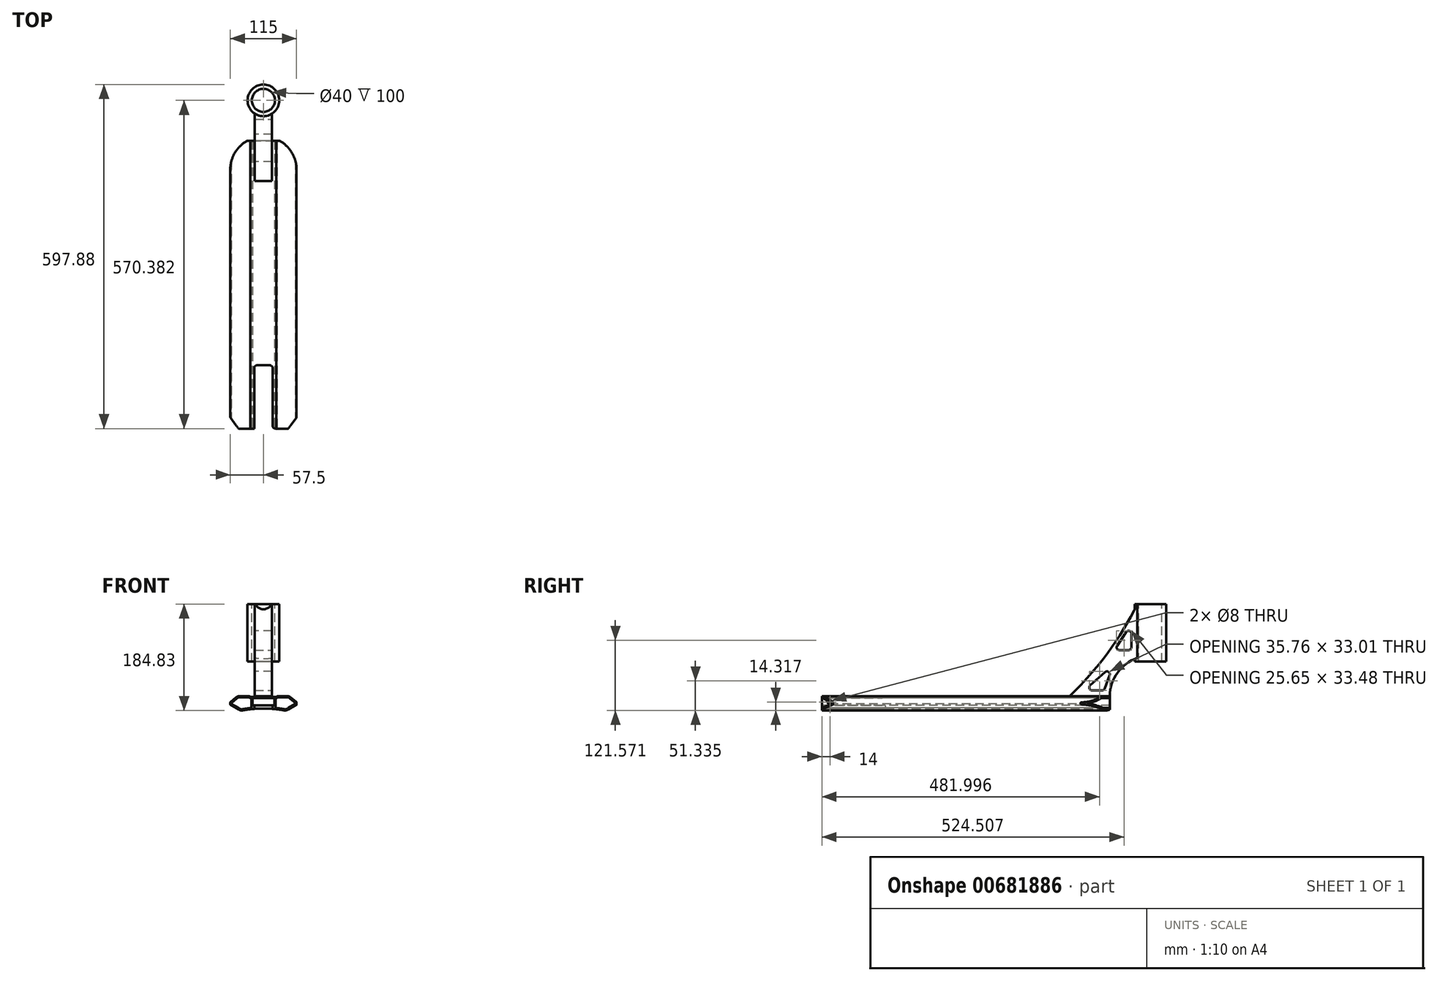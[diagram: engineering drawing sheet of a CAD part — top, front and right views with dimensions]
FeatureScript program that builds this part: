
annotation { "Feature Type Name" : "Feature", "Feature Type Description" : "" }
export const myFeature = defineFeature(function(context is Context, id is Id, definition is map)
    precondition{}
    {
        {
            var Q0;
            Q0=qCreatedBy(makeId("Front.planeOp"),FACE);
            var sketch = newSketch(context, id + "F0", { "sketchPlane" : qUnion([Q0])});
            skLineSegment(sketch, "E0", {"start": v(0, 0) * mm, "end": v(0, 38.3) * mm, "construction": true});
            skLineSegment(sketch, "E1", {"start": v(0, 20.02) * mm, "end": v(22.5, 20.02) * mm});
            skLineSegment(sketch, "E2", {"start": v(22.5, 20.02) * mm, "end": v(22.5, 21.32) * mm});
            skLineSegment(sketch, "E3", {"start": v(22.5, 21.32) * mm, "end": v(44.7, 21.32) * mm});
            skLineSegment(sketch, "E4", {"start": v(44.7, 21.32) * mm, "end": v(57.5, 10.57) * mm});
            skLineSegment(sketch, "E5", {"start": v(57.5, 10.57) * mm, "end": v(57.5, 6.57) * mm});
            skLineSegment(sketch, "E6", {"start": v(57.5, 6.57) * mm, "end": v(39.22, -3.98) * mm});
            skLineSegment(sketch, "E7.MirrorCS", {"start": v(0, 20.02) * mm, "end": v(-22.5, 20.02) * mm});
            skLineSegment(sketch, "E8.MirrorCS", {"start": v(-22.5, 21.32) * mm, "end": v(-44.7, 21.32) * mm});
            skLineSegment(sketch, "E9.MirrorCS", {"start": v(-22.5, 20.02) * mm, "end": v(-22.5, 21.32) * mm});
            skLineSegment(sketch, "E10.MirrorCS", {"start": v(-44.7, 21.32) * mm, "end": v(-57.5, 10.57) * mm});
            skLineSegment(sketch, "E11.MirrorCS", {"start": v(-57.5, 10.57) * mm, "end": v(-57.5, 6.57) * mm});
            skLineSegment(sketch, "E12.MirrorCS", {"start": v(-57.5, 6.57) * mm, "end": v(-39.22, -3.98) * mm});
            skArc(sketch, "E13", {"start": v(39.22, -3.98) * mm, "mid": v(0, -0.1) * mm, "end": v(-39.22, -3.98) * mm});
            skSolve(sketch);
        }
        {
            var Q0;
            Q0 = qSketchRegion(id + "F0", true);
            extrude(context, id + "F1", {"entities" : qUnion([Q0]), "endBound" : BoundingType.SYMMETRIC, "depth" : 500 * mm, "offsetDistance" : 25 * mm});
        }
        {
            var Q0;
            Q0=qCreatedBy(makeId("Front.planeOp"),FACE);
            var sketch = newSketch(context, id + "F2", { "sketchPlane" : qUnion([Q0])});
            skLineSegment(sketch, "E14", {"start": v(-19, 18.02) * mm, "end": v(19, 18.02) * mm});
            skLineSegment(sketch, "E15", {"start": v(19, 18.02) * mm, "end": v(19, 5.02) * mm});
            skLineSegment(sketch, "E16", {"start": v(19, 5.02) * mm, "end": v(-19, 5.02) * mm});
            skLineSegment(sketch, "E17", {"start": v(-19, 5.02) * mm, "end": v(-19, 18.02) * mm});
            skSolve(sketch);
        }
        {
            var Q0;
            Q0 = qSketchRegion(id + "F2", true);
            extrude(context, id + "F3", {"entities" : qUnion([Q0]), "operationType" : NewBodyOperationType.REMOVE, "endBound" : BoundingType.SYMMETRIC, "oppositeDirection" : true, "depth" : 500 * mm, "offsetDistance" : 25 * mm});
        }
        {
            var Q0;
            Q0=makeQuery(id+"F1.opExtrude","SWEPT_EDGE",EDGE,{"disambiguationData":[OSD([sQuery(id+"F0.wireOp",EDGE,"E2"),sQuery(id+"F0.wireOp",EDGE,"E3")])]});
            var Q1;
            Q1=makeQuery(id+"F1.opExtrude","SWEPT_EDGE",EDGE,{"disambiguationData":[OSD([sQuery(id+"F0.wireOp",EDGE,"E9.MirrorCS"),sQuery(id+"F0.wireOp",EDGE,"E8.MirrorCS")])]});
            fillet(context, id + "F4", {"entities" : qUnion([Q0, Q1]), "radius" : 5 * mm, "tangentPropagation" : true, "allowEdgeOverflow" : false});
        }
        {
            var Q0;
            Q0=makeQuery(id+"F1.opExtrude","SWEPT_EDGE",EDGE,{"disambiguationData":[OSD([sQuery(id+"F0.wireOp",EDGE,"E8.MirrorCS"),sQuery(id+"F0.wireOp",EDGE,"E10.MirrorCS")])]});
            var Q1;
            Q1=makeQuery(id+"F1.opExtrude","SWEPT_EDGE",EDGE,{"disambiguationData":[OSD([sQuery(id+"F0.wireOp",EDGE,"E3"),sQuery(id+"F0.wireOp",EDGE,"E4")])]});
            var Q2;
            Q2=makeQuery(id+"F1.opExtrude","SWEPT_EDGE",EDGE,{"disambiguationData":[OSD([sQuery(id+"F0.wireOp",EDGE,"E12.MirrorCS"),sQuery(id+"F0.wireOp",EDGE,"E13")])]});
            var Q3;
            Q3=makeQuery(id+"F1.opExtrude","SWEPT_EDGE",EDGE,{"disambiguationData":[OSD([sQuery(id+"F0.wireOp",EDGE,"E6"),sQuery(id+"F0.wireOp",EDGE,"E13")])]});
            fillet(context, id + "F5", {"entities" : qUnion([Q0, Q1, Q2, Q3]), "radius" : 9 * mm, "tangentPropagation" : true, "allowEdgeOverflow" : false});
        }
        {
            var Q0;
            Q0=makeQuery(id+"F1.opExtrude","SWEPT_EDGE",EDGE,{"disambiguationData":[OSD([sQuery(id+"F0.wireOp",EDGE,"E6"),sQuery(id+"F0.wireOp",EDGE,"E5")])]});
            var Q1;
            Q1=makeQuery(id+"F1.opExtrude","SWEPT_EDGE",EDGE,{"disambiguationData":[OSD([sQuery(id+"F0.wireOp",EDGE,"E4"),sQuery(id+"F0.wireOp",EDGE,"E5")])]});
            var Q2;
            Q2=makeQuery(id+"F1.opExtrude","SWEPT_EDGE",EDGE,{"disambiguationData":[OSD([sQuery(id+"F0.wireOp",EDGE,"E10.MirrorCS"),sQuery(id+"F0.wireOp",EDGE,"E11.MirrorCS")])]});
            var Q3;
            Q3=makeQuery(id+"F1.opExtrude","SWEPT_EDGE",EDGE,{"disambiguationData":[OSD([sQuery(id+"F0.wireOp",EDGE,"E11.MirrorCS"),sQuery(id+"F0.wireOp",EDGE,"E12.MirrorCS")])]});
            fillet(context, id + "F6", {"entities" : qUnion([Q0, Q1, Q2, Q3]), "radius" : 1 * mm, "tangentPropagation" : true, "allowEdgeOverflow" : false});
        }
        {
            var Q0;
            Q0=makeQuery(id+"F1.opExtrude","CAP_FACE",FACE,{"disambiguationData":[OSD([sQuery(id+"F0.wireOp",EDGE,"E1"),sQuery(id+"F0.wireOp",EDGE,"E2"),sQuery(id+"F0.wireOp",EDGE,"E3"),sQuery(id+"F0.wireOp",EDGE,"E4"),sQuery(id+"F0.wireOp",EDGE,"E6"),sQuery(id+"F0.wireOp",EDGE,"E7.MirrorCS"),sQuery(id+"F0.wireOp",EDGE,"E9.MirrorCS"),sQuery(id+"F0.wireOp",EDGE,"E8.MirrorCS"),sQuery(id+"F0.wireOp",EDGE,"E10.MirrorCS"),sQuery(id+"F0.wireOp",EDGE,"E11.MirrorCS"),sQuery(id+"F0.wireOp",EDGE,"E12.MirrorCS"),sQuery(id+"F0.wireOp",EDGE,"E5"),sQuery(id+"F0.wireOp",EDGE,"E13")])],"isStart":false});
            var sketch = newSketch(context, id + "F7", { "sketchPlane" : qUnion([Q0])});
            skArc(sketch, "E18.0", {"start": v(-21, 0.8) * mm, "mid": v(-28.7, -0.15) * mm, "end": v(-36.36, -1.4) * mm});
            skArc(sketch, "E18.1", {"start": v(-41.12, -0.57) * mm, "mid": v(-38.81, -1.4) * mm, "end": v(-36.36, -1.4) * mm});
            skLineSegment(sketch, "E18.2", {"start": v(-55.5, 7.73) * mm, "end": v(-41.12, -0.57) * mm});
            skArc(sketch, "E18.4", {"start": v(-23.4, 18.02) * mm, "mid": v(-24.47, 18.97) * mm, "end": v(-25.86, 19.32) * mm});
            skLineSegment(sketch, "E18.5", {"start": v(-25.86, 19.32) * mm, "end": v(-41.42, 19.32) * mm});
            skArc(sketch, "E18.6", {"start": v(-41.42, 19.32) * mm, "mid": v(-43.81, 18.9) * mm, "end": v(-45.92, 17.68) * mm});
            skLineSegment(sketch, "E18.7", {"start": v(-45.92, 17.68) * mm, "end": v(-55.76, 9.42) * mm});
            skLineSegment(sketch, "E19.0", {"start": v(-21, 0.8) * mm, "end": v(-21, 18.02) * mm});
            skLineSegment(sketch, "E20.0", {"start": v(-23.4, 18.02) * mm, "end": v(-21, 18.02) * mm});
            skPoint(sketch, "E21.startSnap0", {"position": v(-55.5, 8.69) * mm});
            skArc(sketch, "E22", {"start": v(-55.76, 9.42) * mm, "mid": v(-56.1, 8.5) * mm, "end": v(-55.5, 7.73) * mm});
            skLineSegment(sketch, "E23", {"start": v(0, 55.9) * mm, "end": v(0, 0) * mm, "construction": true});
            skLineSegment(sketch, "E24.MirrorCS", {"start": v(23.4, 18.02) * mm, "end": v(21, 18.02) * mm});
            skLineSegment(sketch, "E25.MirrorCS", {"start": v(21, 0.8) * mm, "end": v(21, 18.02) * mm});
            skArc(sketch, "E26.MirrorCS", {"start": v(21, 0.8) * mm, "mid": v(28.7, -0.15) * mm, "end": v(36.36, -1.4) * mm});
            skArc(sketch, "E27.MirrorCS", {"start": v(41.12, -0.57) * mm, "mid": v(38.81, -1.4) * mm, "end": v(36.36, -1.4) * mm});
            skLineSegment(sketch, "E28.MirrorCS", {"start": v(55.5, 7.73) * mm, "end": v(41.12, -0.57) * mm});
            skArc(sketch, "E29.MirrorCS", {"start": v(55.76, 9.42) * mm, "mid": v(56.1, 8.5) * mm, "end": v(55.5, 7.73) * mm});
            skLineSegment(sketch, "E30.MirrorCS", {"start": v(45.92, 17.68) * mm, "end": v(55.76, 9.42) * mm});
            skArc(sketch, "E31.MirrorCS", {"start": v(41.42, 19.32) * mm, "mid": v(43.81, 18.9) * mm, "end": v(45.92, 17.68) * mm});
            skLineSegment(sketch, "E32.MirrorCS", {"start": v(25.86, 19.32) * mm, "end": v(41.42, 19.32) * mm});
            skArc(sketch, "E33.MirrorCS", {"start": v(23.4, 18.02) * mm, "mid": v(24.47, 18.97) * mm, "end": v(25.86, 19.32) * mm});
            skSolve(sketch);
        }
        {
            var Q0;
            Q0=makeQuery(id+"F7.imprint","IMPRINT",FACE,{"disambiguationData":[TD([[makeQuery(id+"F7.imprint","IMPRINT",EDGE,{"derivedFrom":sQuery(id+"F7.wireOp",EDGE,"E24.MirrorCS")}),1.0]])]});
            var Q1;
            Q1=makeQuery(id+"F7.imprint","IMPRINT",FACE,{"disambiguationData":[TD([[makeQuery(id+"F7.imprint","IMPRINT",EDGE,{"derivedFrom":sQuery(id+"F7.wireOp",EDGE,"E18.0")}),-1.0]])]});
            extrude(context, id + "F8", {"entities" : qUnion([Q0, Q1]), "operationType" : NewBodyOperationType.REMOVE, "endBound" : BoundingType.THROUGH_ALL, "oppositeDirection" : true, "depth" : 25 * mm, "offsetDistance" : 25 * mm});
        }
        {
            var Q0;
            Q0=qCreatedBy(makeId("Top.planeOp"),FACE);
            var sketch = newSketch(context, id + "F9", { "sketchPlane" : qUnion([Q0])});
            skArc(sketch, "E34", {"start": v(57.5, 199.3) * mm, "mid": v(0.35, 257.5) * mm, "end": v(-57.5, 200) * mm});
            skLineSegment(sketch, "E35", {"start": v(-57.5, 200) * mm, "end": v(-57.5, 280) * mm});
            skLineSegment(sketch, "E36", {"start": v(58.48, 280) * mm, "end": v(57.5, 199.3) * mm});
            skLineSegment(sketch, "E37", {"start": v(-57.5, 280) * mm, "end": v(58.48, 280) * mm});
            skSolve(sketch);
        }
        {
            var Q0;
            Q0 = qSketchRegion(id + "F9", true);
            extrude(context, id + "F10", {"entities" : qUnion([Q0]), "operationType" : NewBodyOperationType.REMOVE, "endBound" : BoundingType.THROUGH_ALL, "depth" : 25 * mm, "offsetDistance" : 25 * mm, "hasSecondDirection" : true, "secondDirectionBound" : SecondDirectionBoundingType.THROUGH_ALL, "secondDirectionOppositeDirection" : true, "secondDirectionDepth" : 25 * mm});
        }
        {
            var Q0;
            Q0=qCreatedBy(makeId("Top.planeOp"),FACE);
            var sketch = newSketch(context, id + "F11", { "sketchPlane" : qUnion([Q0])});
            skLineSegment(sketch, "E38", {"start": v(-68, -216) * mm, "end": v(-68, -346) * mm});
            skLineSegment(sketch, "E39", {"start": v(-68, -346) * mm, "end": v(68, -346) * mm});
            skLineSegment(sketch, "E40", {"start": v(68, -346) * mm, "end": v(68, -216) * mm});
            skLineSegment(sketch, "E41", {"start": v(68, -216) * mm, "end": v(43.3, -250) * mm});
            skLineSegment(sketch, "E42", {"start": v(43.3, -250) * mm, "end": v(16, -250) * mm});
            skLineSegment(sketch, "E43", {"start": v(16, -250) * mm, "end": v(16, -140) * mm});
            skLineSegment(sketch, "E44", {"start": v(16, -140) * mm, "end": v(-16, -140) * mm});
            skLineSegment(sketch, "E45", {"start": v(-16, -140) * mm, "end": v(-16, -250) * mm});
            skLineSegment(sketch, "E46", {"start": v(-16, -250) * mm, "end": v(-43.3, -250) * mm});
            skLineSegment(sketch, "E47", {"start": v(-43.3, -250) * mm, "end": v(-68, -216) * mm});
            skSolve(sketch);
        }
        {
            var Q0;
            Q0 = qSketchRegion(id + "F11", true);
            extrude(context, id + "F12", {"entities" : qUnion([Q0]), "operationType" : NewBodyOperationType.REMOVE, "endBound" : BoundingType.THROUGH_ALL, "depth" : 25 * mm, "offsetDistance" : 25 * mm, "hasSecondDirection" : true, "secondDirectionBound" : SecondDirectionBoundingType.THROUGH_ALL, "secondDirectionOppositeDirection" : true, "secondDirectionDepth" : 25 * mm});
        }
        {
            var Q0;
            {var subQ2=sQuery(id+"F11.wireOp",EDGE,"E45");Q0=makeQuery(id+"F12.boolean.opBoolean","COPY",EDGE,{"disambiguationData":[TD([makeQuery(id+"F3.boolean.opBoolean","COPY",FACE,{"derivedFrom":makeQuery(id+"F3.opExtrude","SWEPT_FACE",FACE,{"disambiguationData":[OSD([sQuery(id+"F2.wireOp",EDGE,"E14")])]})})])],"derivedFrom":makeQuery(id+"F12.opExtrude","SWEPT_EDGE",EDGE,{"disambiguationData":[OSD([subQ2,sQuery(id+"F11.wireOp",EDGE,"E46")])]})});}
            var Q1;
            {var subQ0=sQuery(id+"F0.wireOp",EDGE,"E13");var subQ1=sQuery(id+"F11.wireOp",EDGE,"E45");Q1=makeQuery(id+"F12.boolean.opBoolean","COPY",EDGE,{"disambiguationData":[TD([makeQuery(id+"F1.opExtrude","SWEPT_FACE",FACE,{"disambiguationData":[OSD([subQ0])]})])],"derivedFrom":makeQuery(id+"F12.opExtrude","SWEPT_EDGE",EDGE,{"disambiguationData":[OSD([subQ1,sQuery(id+"F11.wireOp",EDGE,"E46")])]})});}
            var Q2;
            {var subQ0=sQuery(id+"F11.wireOp",EDGE,"E44");var subQ1=sQuery(id+"F11.wireOp",EDGE,"E45");Q2=makeQuery(id+"F12.boolean.opBoolean","COPY",EDGE,{"disambiguationData":[TD([makeQuery(id+"F3.boolean.opBoolean","COPY",FACE,{"derivedFrom":makeQuery(id+"F3.opExtrude","SWEPT_FACE",FACE,{"disambiguationData":[OSD([sQuery(id+"F2.wireOp",EDGE,"E14")])]})})])],"derivedFrom":makeQuery(id+"F12.opExtrude","SWEPT_EDGE",EDGE,{"disambiguationData":[OSD([subQ0,subQ1])]})});}
            var Q3;
            {var subQ0=sQuery(id+"F11.wireOp",EDGE,"E44");var subQ1=sQuery(id+"F11.wireOp",EDGE,"E45");Q3=makeQuery(id+"F12.boolean.opBoolean","COPY",EDGE,{"disambiguationData":[TD([makeQuery(id+"F1.opExtrude","SWEPT_FACE",FACE,{"disambiguationData":[OSD([sQuery(id+"F0.wireOp",EDGE,"E13")])]})])],"derivedFrom":makeQuery(id+"F12.opExtrude","SWEPT_EDGE",EDGE,{"disambiguationData":[OSD([subQ0,subQ1])]})});}
            var Q4;
            {var subQ0=sQuery(id+"F11.wireOp",EDGE,"E43");var subQ1=sQuery(id+"F11.wireOp",EDGE,"E44");Q4=makeQuery(id+"F12.boolean.opBoolean","COPY",EDGE,{"disambiguationData":[TD([makeQuery(id+"F1.opExtrude","SWEPT_FACE",FACE,{"disambiguationData":[OSD([sQuery(id+"F0.wireOp",EDGE,"E13")])]})])],"derivedFrom":makeQuery(id+"F12.opExtrude","SWEPT_EDGE",EDGE,{"disambiguationData":[OSD([subQ0,subQ1])]})});}
            var Q5;
            {var subQ0=sQuery(id+"F11.wireOp",EDGE,"E43");var subQ1=sQuery(id+"F11.wireOp",EDGE,"E44");Q5=makeQuery(id+"F12.boolean.opBoolean","COPY",EDGE,{"disambiguationData":[TD([makeQuery(id+"F3.boolean.opBoolean","COPY",FACE,{"derivedFrom":makeQuery(id+"F3.opExtrude","SWEPT_FACE",FACE,{"disambiguationData":[OSD([sQuery(id+"F2.wireOp",EDGE,"E14")])]})})])],"derivedFrom":makeQuery(id+"F12.opExtrude","SWEPT_EDGE",EDGE,{"disambiguationData":[OSD([subQ0,subQ1])]})});}
            var Q6;
            {var subQ2=sQuery(id+"F11.wireOp",EDGE,"E43");Q6=makeQuery(id+"F12.boolean.opBoolean","COPY",EDGE,{"disambiguationData":[TD([makeQuery(id+"F3.boolean.opBoolean","COPY",FACE,{"derivedFrom":makeQuery(id+"F3.opExtrude","SWEPT_FACE",FACE,{"disambiguationData":[OSD([sQuery(id+"F2.wireOp",EDGE,"E14")])]})})])],"derivedFrom":makeQuery(id+"F12.opExtrude","SWEPT_EDGE",EDGE,{"disambiguationData":[OSD([sQuery(id+"F11.wireOp",EDGE,"E42"),subQ2])]})});}
            var Q7;
            {var subQ0=sQuery(id+"F0.wireOp",EDGE,"E13");var subQ1=sQuery(id+"F11.wireOp",EDGE,"E43");Q7=makeQuery(id+"F12.boolean.opBoolean","COPY",EDGE,{"disambiguationData":[TD([makeQuery(id+"F1.opExtrude","SWEPT_FACE",FACE,{"disambiguationData":[OSD([subQ0])]})])],"derivedFrom":makeQuery(id+"F12.opExtrude","SWEPT_EDGE",EDGE,{"disambiguationData":[OSD([sQuery(id+"F11.wireOp",EDGE,"E42"),subQ1])]})});}
            fillet(context, id + "F13", {"entities" : qUnion([Q0, Q1, Q2, Q3, Q4, Q5, Q6, Q7]), "radius" : 5 * mm, "tangentPropagation" : true, "allowEdgeOverflow" : false});
        }
        {
            var Q0;
            Q0=qCreatedBy(makeId("Right.planeOp"),FACE);
            var sketch = newSketch(context, id + "F14", { "sketchPlane" : qUnion([Q0])});
            skLineSegment(sketch, "E48", {"start": v(250, 21.32) * mm, "end": v(180, 21.32) * mm});
            skArc(sketch, "E49", {"start": v(297.38, 87.56) * mm, "mid": v(263.06, 62.04) * mm, "end": v(250, 21.32) * mm});
            skLineSegment(sketch, "E50", {"start": v(297.38, 87.56) * mm, "end": v(297.38, 81.32) * mm});
            skLineSegment(sketch, "E51", {"start": v(297.38, 81.32) * mm, "end": v(343.38, 81.32) * mm});
            skLineSegment(sketch, "E52", {"start": v(343.38, 81.32) * mm, "end": v(343.38, 181.32) * mm});
            skLineSegment(sketch, "E53", {"start": v(343.38, 181.32) * mm, "end": v(297.38, 181.32) * mm});
            skArc(sketch, "E54", {"start": v(180, 21.32) * mm, "mid": v(245.97, 95.98) * mm, "end": v(297.38, 181.32) * mm});
            skSolve(sketch);
        }
        {
            var Q0;
            Q0 = qSketchRegion(id + "F14", true);
            extrude(context, id + "F15", {"entities" : qUnion([Q0]), "operationType" : NewBodyOperationType.ADD, "endBound" : BoundingType.SYMMETRIC, "depth" : 30 * mm, "offsetDistance" : 25 * mm});
        }
        {
            var Q0;
            Q0=makeQuery(id+"F15.opExtrude","SWEPT_FACE",FACE,{"disambiguationData":[OSD([sQuery(id+"F14.wireOp",EDGE,"E53")])]});
            var sketch = newSketch(context, id + "F16", { "sketchPlane" : qUnion([Q0])});
            skCircle(sketch, "E55", {"center": v(0, 320.38) * mm, "radius": 27.5 * mm});
            skPoint(sketch, "E56.positionSnap0", {"position": v(15, 320.38) * mm});
            skSolve(sketch);
        }
        {
            var Q0;
            Q0 = qSketchRegion(id + "F16", true);
            var Q1;
            Q1=makeQuery(id+"F15.opExtrude","SWEPT_FACE",FACE,{"disambiguationData":[OSD([sQuery(id+"F14.wireOp",EDGE,"E51")])]});
            extrude(context, id + "F17", {"entities" : qUnion([Q0]), "operationType" : NewBodyOperationType.ADD, "endBound" : BoundingType.UP_TO_SURFACE, "oppositeDirection" : true, "depth" : 25 * mm, "endBoundEntityFace" : qUnion([Q1]), "offsetDistance" : 25 * mm});
        }
        {
            var Q0;
            Q0=makeQuery(id+"F17.boolean.opBoolean","MERGE",FACE,{"derivedFrom":[makeQuery(id+"F15.opExtrude","SWEPT_FACE",FACE,{"disambiguationData":[OSD([sQuery(id+"F14.wireOp",EDGE,"E53")])]}),makeQuery(id+"F17.opExtrude","CAP_FACE",FACE,{"disambiguationData":[OSD([sQuery(id+"F16.wireOp",EDGE,"E55")])],"isStart":true})]});
            var sketch = newSketch(context, id + "F18", { "sketchPlane" : qUnion([Q0])});
            skPoint(sketch, "E57", {"position": v(0, 320.38) * mm});
            skSolve(sketch);
        }
        {
            var Q0;
            Q0=sQuery(id+"F18.wireOp",VERTEX,"E57");
            var Q1;
            Q1=makeQuery(id+"F15.opExtrude","SWEPT_BODY",BODY,{"disambiguationData":[OSD([sQuery(id+"F14.wireOp",EDGE,"E48"),sQuery(id+"F14.wireOp",EDGE,"E49"),sQuery(id+"F14.wireOp",EDGE,"E50"),sQuery(id+"F14.wireOp",EDGE,"E51"),sQuery(id+"F14.wireOp",EDGE,"E52"),sQuery(id+"F14.wireOp",EDGE,"E53"),sQuery(id+"F14.wireOp",EDGE,"E54")])]});
            hole(context, id + "F19", {"style" : HoleStyle.SIMPLE, "endStyle" : HoleEndStyle.THROUGH, "holeDiameter" : 40 * mm, "majorDiameter" : 5 * mm, "isTappedThrough" : true, "tappedDepth" : 12 * mm, "tapClearance" : 3, "locations" : qUnion([Q0]), "scope" : qUnion([Q1])});
        }
        {
            var Q0;
            Q0=makeQuery(id+"F8.boolean.opBoolean","COPY",FACE,{"derivedFrom":makeQuery(id+"F8.opExtrude","SWEPT_FACE",FACE,{"disambiguationData":[OSD([sQuery(id+"F7.wireOp",EDGE,"E25.MirrorCS")])]})});
            var sketch = newSketch(context, id + "F20", { "sketchPlane" : qUnion([Q0])});
            skPoint(sketch, "E58.positionSnap0", {"position": v(-250, 9.41) * mm});
            skPoint(sketch, "E59", {"position": v(-236, 10.8) * mm});
            skSolve(sketch);
        }
        {
            var Q0;
            Q0=sQuery(id+"F20.wireOp",VERTEX,"E59");
            var Q1;
            Q1=makeQuery(id+"F1.opExtrude","SWEPT_BODY",BODY,{"disambiguationData":[OSD([sQuery(id+"F0.wireOp",EDGE,"E1"),sQuery(id+"F0.wireOp",EDGE,"E2"),sQuery(id+"F0.wireOp",EDGE,"E3"),sQuery(id+"F0.wireOp",EDGE,"E4"),sQuery(id+"F0.wireOp",EDGE,"E6"),sQuery(id+"F0.wireOp",EDGE,"E7.MirrorCS"),sQuery(id+"F0.wireOp",EDGE,"E9.MirrorCS"),sQuery(id+"F0.wireOp",EDGE,"E8.MirrorCS"),sQuery(id+"F0.wireOp",EDGE,"E10.MirrorCS"),sQuery(id+"F0.wireOp",EDGE,"E11.MirrorCS"),sQuery(id+"F0.wireOp",EDGE,"E12.MirrorCS"),sQuery(id+"F0.wireOp",EDGE,"E5"),sQuery(id+"F0.wireOp",EDGE,"E13")])]});
            hole(context, id + "F21", {"style" : HoleStyle.SIMPLE, "endStyle" : HoleEndStyle.BLIND, "holeDiameter" : 8 * mm, "majorDiameter" : 5 * mm, "holeDepth" : 45 * mm, "isTappedThrough" : true, "tappedDepth" : 12 * mm, "tapClearance" : 3, "locations" : qUnion([Q0]), "scope" : qUnion([Q1])});
        }
        {
            var Q0;
            Q0=makeQuery(id+"F15.opExtrude","CAP_FACE",FACE,{"disambiguationData":[OSD([sQuery(id+"F14.wireOp",EDGE,"E48"),sQuery(id+"F14.wireOp",EDGE,"E49"),sQuery(id+"F14.wireOp",EDGE,"E50"),sQuery(id+"F14.wireOp",EDGE,"E51"),sQuery(id+"F14.wireOp",EDGE,"E52"),sQuery(id+"F14.wireOp",EDGE,"E53"),sQuery(id+"F14.wireOp",EDGE,"E54")])],"isStart":false});
            var sketch = newSketch(context, id + "F22", { "sketchPlane" : qUnion([Q0])});
            skLineSegment(sketch, "E60", {"start": v(257.33, 101.32) * mm, "end": v(287.33, 146.32) * mm});
            skLineSegment(sketch, "E61", {"start": v(287.33, 146.32) * mm, "end": v(287.33, 101.32) * mm});
            skLineSegment(sketch, "E62", {"start": v(287.33, 101.32) * mm, "end": v(257.33, 101.32) * mm});
            skLineSegment(sketch, "E63", {"start": v(206, 31.32) * mm, "end": v(240, 31.32) * mm});
            skLineSegment(sketch, "E64", {"start": v(240, 31.32) * mm, "end": v(256.38, 76.32) * mm});
            skLineSegment(sketch, "E65", {"start": v(256.38, 76.32) * mm, "end": v(206, 31.32) * mm});
            skSolve(sketch);
        }
        {
            var Q0;
            Q0 = qSketchRegion(id + "F22", true);
            extrude(context, id + "F23", {"entities" : qUnion([Q0]), "operationType" : NewBodyOperationType.REMOVE, "endBound" : BoundingType.THROUGH_ALL, "oppositeDirection" : true, "depth" : 25 * mm, "offsetDistance" : 25 * mm});
        }
        {
            var Q0;
            Q0=makeQuery(id+"F23.boolean.opBoolean","COPY",EDGE,{"derivedFrom":makeQuery(id+"F23.opExtrude","SWEPT_EDGE",EDGE,{"disambiguationData":[OSD([sQuery(id+"F22.wireOp",EDGE,"E60"),sQuery(id+"F22.wireOp",EDGE,"E61")])]})});
            var Q1;
            Q1=makeQuery(id+"F23.boolean.opBoolean","COPY",EDGE,{"derivedFrom":makeQuery(id+"F23.opExtrude","SWEPT_EDGE",EDGE,{"disambiguationData":[OSD([sQuery(id+"F22.wireOp",EDGE,"E60"),sQuery(id+"F22.wireOp",EDGE,"E62")])]})});
            var Q2;
            Q2=makeQuery(id+"F23.boolean.opBoolean","COPY",EDGE,{"derivedFrom":makeQuery(id+"F23.opExtrude","SWEPT_EDGE",EDGE,{"disambiguationData":[OSD([sQuery(id+"F22.wireOp",EDGE,"E61"),sQuery(id+"F22.wireOp",EDGE,"E62")])]})});
            var Q3;
            Q3=makeQuery(id+"F23.boolean.opBoolean","COPY",EDGE,{"derivedFrom":makeQuery(id+"F23.opExtrude","SWEPT_EDGE",EDGE,{"disambiguationData":[OSD([sQuery(id+"F22.wireOp",EDGE,"E63"),sQuery(id+"F22.wireOp",EDGE,"E64")])]})});
            var Q4;
            Q4=makeQuery(id+"F23.boolean.opBoolean","COPY",EDGE,{"derivedFrom":makeQuery(id+"F23.opExtrude","SWEPT_EDGE",EDGE,{"disambiguationData":[OSD([sQuery(id+"F22.wireOp",EDGE,"E64"),sQuery(id+"F22.wireOp",EDGE,"E65")])]})});
            var Q5;
            Q5=makeQuery(id+"F23.boolean.opBoolean","COPY",EDGE,{"derivedFrom":makeQuery(id+"F23.opExtrude","SWEPT_EDGE",EDGE,{"disambiguationData":[OSD([sQuery(id+"F22.wireOp",EDGE,"E63"),sQuery(id+"F22.wireOp",EDGE,"E65")])]})});
            fillet(context, id + "F24", {"entities" : qUnion([Q0, Q1, Q2, Q3, Q4, Q5]), "radius" : 5 * mm, "tangentPropagation" : true, "allowEdgeOverflow" : false});
        }
    });
